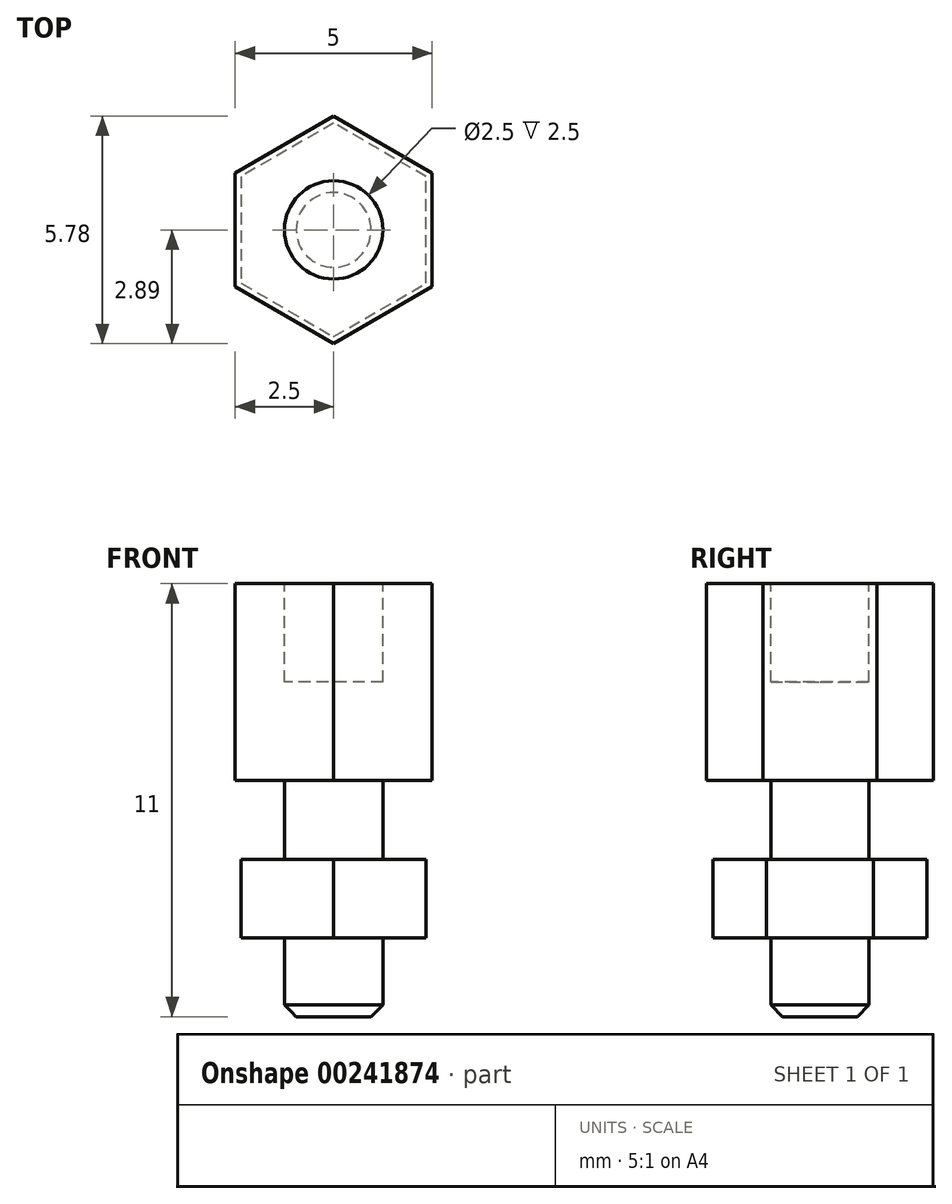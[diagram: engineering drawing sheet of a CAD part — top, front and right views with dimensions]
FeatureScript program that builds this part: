
annotation { "Feature Type Name" : "Feature", "Feature Type Description" : "" }
export const myFeature = defineFeature(function(context is Context, id is Id, definition is map)
    precondition{}
    {
        {
            var Q0;
            Q0=qCreatedBy(makeId("Top.planeOp"),FACE);
            var sketch = newSketch(context, id + "F0", { "sketchPlane" : qUnion([Q0])});
            skCircle(sketch, "E0.cCircle", {"center": v(0, 0) * mm, "radius": 2.5 * mm, "construction": true});
            skLineSegment(sketch, "E0.0", {"start": v(0, 2.89) * mm, "end": v(2.5, 1.44) * mm});
            skLineSegment(sketch, "E0.1", {"start": v(2.5, 1.44) * mm, "end": v(2.5, -1.44) * mm});
            skLineSegment(sketch, "E0.2", {"start": v(2.5, -1.44) * mm, "end": v(0, -2.89) * mm});
            skLineSegment(sketch, "E0.3", {"start": v(0, -2.89) * mm, "end": v(-2.5, -1.44) * mm});
            skLineSegment(sketch, "E0.4", {"start": v(-2.5, -1.44) * mm, "end": v(-2.5, 1.44) * mm});
            skLineSegment(sketch, "E0.5", {"start": v(-2.5, 1.44) * mm, "end": v(0, 2.89) * mm});
            skPoint(sketch, "E0.0.midPoint", {"position": v(1.25, 2.17) * mm});
            skSolve(sketch);
        }
        {
            var Q0;
            Q0 = qSketchRegion(id + "F0", true);
            extrude(context, id + "F1", {"entities" : qUnion([Q0]), "oppositeDirection" : true, "depth" : 5 * mm});
        }
        {
            var Q0;
            Q0=makeQuery(id+"F1.opExtrude","CAP_FACE",FACE,{"disambiguationData":[OSD([sQuery(id+"F0.wireOp",EDGE,"E0.0"),sQuery(id+"F0.wireOp",EDGE,"E0.1"),sQuery(id+"F0.wireOp",EDGE,"E0.2"),sQuery(id+"F0.wireOp",EDGE,"E0.3"),sQuery(id+"F0.wireOp",EDGE,"E0.4"),sQuery(id+"F0.wireOp",EDGE,"E0.5")])],"isStart":false});
            var sketch = newSketch(context, id + "F2", { "sketchPlane" : qUnion([Q0])});
            skCircle(sketch, "E1", {"center": v(0, 0) * mm, "radius": 1.25 * mm});
            skSolve(sketch);
        }
        {
            var Q0;
            Q0 = qSketchRegion(id + "F2", true);
            extrude(context, id + "F3", {"entities" : qUnion([Q0]), "operationType" : NewBodyOperationType.ADD, "depth" : 6 * mm});
        }
        {
            var Q0;
            Q0=makeQuery(id+"F1.opExtrude","CAP_FACE",FACE,{"disambiguationData":[OSD([sQuery(id+"F0.wireOp",EDGE,"E0.0"),sQuery(id+"F0.wireOp",EDGE,"E0.1"),sQuery(id+"F0.wireOp",EDGE,"E0.2"),sQuery(id+"F0.wireOp",EDGE,"E0.3"),sQuery(id+"F0.wireOp",EDGE,"E0.4"),sQuery(id+"F0.wireOp",EDGE,"E0.5")])],"isStart":true});
            var sketch = newSketch(context, id + "F4", { "sketchPlane" : qUnion([Q0])});
            skCircle(sketch, "E2.0", {"center": v(0, 0) * mm, "radius": 1.25 * mm});
            skSolve(sketch);
        }
        {
            var Q0;
            Q0 = qSketchRegion(id + "F4", true);
            extrude(context, id + "F5", {"entities" : qUnion([Q0]), "operationType" : NewBodyOperationType.REMOVE, "oppositeDirection" : true, "depth" : 2.5 * mm});
        }
        {
            var Q0;
            Q0=makeQuery(id+"F3.opExtrude","CAP_EDGE",EDGE,{"disambiguationData":[OSD([sQuery(id+"F2.wireOp",EDGE,"E1")])],"isStart":false});
            chamfer(context, id + "F6", {"entities" : qUnion([Q0]), "width" : 0.3 * mm, "tangentPropagation" : true});
        }
        {
            var Q0;
            Q0=makeQuery(id+"F1.opExtrude","CAP_FACE",FACE,{"disambiguationData":[OSD([sQuery(id+"F0.wireOp",EDGE,"E0.0"),sQuery(id+"F0.wireOp",EDGE,"E0.1"),sQuery(id+"F0.wireOp",EDGE,"E0.2"),sQuery(id+"F0.wireOp",EDGE,"E0.3"),sQuery(id+"F0.wireOp",EDGE,"E0.4"),sQuery(id+"F0.wireOp",EDGE,"E0.5")])],"isStart":false});
            cPlane(context, id + "F7", {"entities" : qUnion([Q0]), "cplaneType" : CPlaneType.OFFSET, "offset" : 2 * mm, "width" : 150 * mm, "height" : 150 * mm});
        }
        {
            var Q0;
            Q0=qCreatedBy(id+"F7.planeOp",FACE);
            var sketch = newSketch(context, id + "F8", { "sketchPlane" : qUnion([Q0])});
            skCircle(sketch, "E3.cCircle", {"center": v(0, 0) * mm, "radius": 2.35 * mm, "construction": true});
            skLineSegment(sketch, "E3.0", {"start": v(-2.35, 1.36) * mm, "end": v(0, 2.71) * mm});
            skLineSegment(sketch, "E3.1", {"start": v(0, 2.71) * mm, "end": v(2.35, 1.36) * mm});
            skLineSegment(sketch, "E3.2", {"start": v(2.35, 1.36) * mm, "end": v(2.35, -1.36) * mm});
            skLineSegment(sketch, "E3.3", {"start": v(2.35, -1.36) * mm, "end": v(0, -2.71) * mm});
            skLineSegment(sketch, "E3.4", {"start": v(0, -2.71) * mm, "end": v(-2.35, -1.36) * mm});
            skLineSegment(sketch, "E3.5", {"start": v(-2.35, -1.36) * mm, "end": v(-2.35, 1.36) * mm});
            skPoint(sketch, "E3.0.midPoint", {"position": v(-1.18, 2.04) * mm});
            skCircle(sketch, "E4", {"center": v(0, 0) * mm, "radius": 1.25 * mm});
            skSolve(sketch);
        }
        {
            var Q0;
            Q0 = qSketchRegion(id + "F8", true);
            extrude(context, id + "F9", {"entities" : qUnion([Q0]), "operationType" : NewBodyOperationType.ADD, "depth" : 2 * mm});
        }
    });
